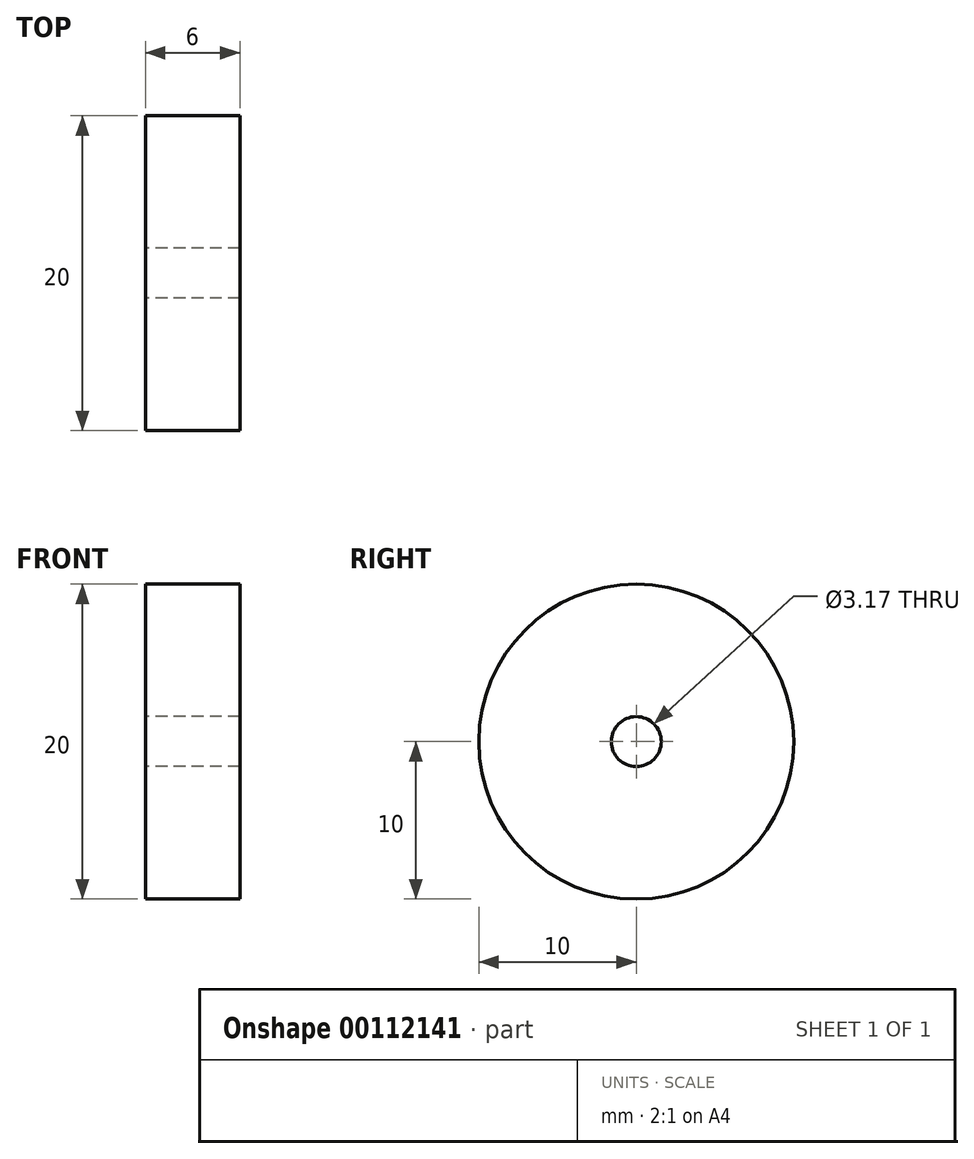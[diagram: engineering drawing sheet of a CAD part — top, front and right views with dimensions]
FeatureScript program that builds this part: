
annotation { "Feature Type Name" : "Feature", "Feature Type Description" : "" }
export const myFeature = defineFeature(function(context is Context, id is Id, definition is map)
    precondition{}
    {
        {
            var Q0;
            Q0=qCreatedBy(makeId("Right.planeOp"),FACE);
            var sketch = newSketch(context, id + "F0", { "sketchPlane" : qUnion([Q0])});
            skCircle(sketch, "E0", {"center": v(0, 0) * mm, "radius": 10 * mm});
            skCircle(sketch, "E1", {"center": v(0, 0) * mm, "radius": 1.59 * mm});
            skSolve(sketch);
        }
        {
            var Q0;
            Q0=makeQuery(id+"F0.imprint","IMPRINT",FACE,{"disambiguationData":[TD([[makeQuery(id+"F0.imprint","IMPRINT",EDGE,{"derivedFrom":sQuery(id+"F0.wireOp",EDGE,"E0")}),1.0]])]});
            extrude(context, id + "F1", {"entities" : qUnion([Q0]), "depth" : 6 * mm});
        }
    });
